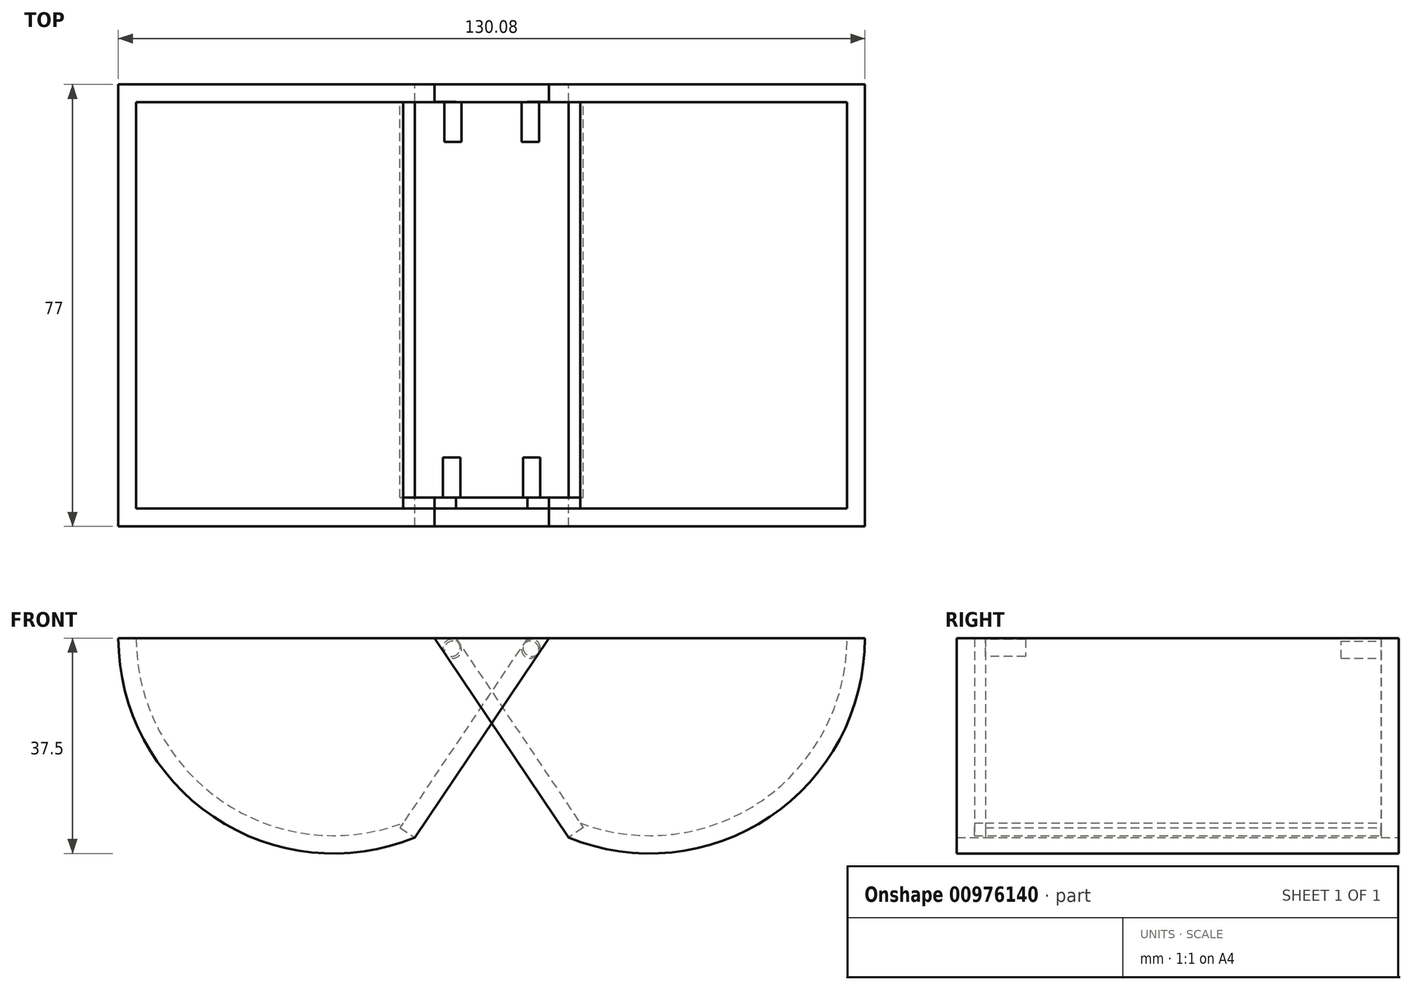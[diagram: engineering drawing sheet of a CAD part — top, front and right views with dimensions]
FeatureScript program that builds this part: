
annotation { "Feature Type Name" : "Feature", "Feature Type Description" : "" }
export const myFeature = defineFeature(function(context is Context, id is Id, definition is map)
    precondition{}
    {
        {
            var Q0;
            Q0=qCreatedBy(makeId("Front.planeOp"),FACE);
            var sketch = newSketch(context, id + "F0", { "sketchPlane" : qUnion([Q0])});
            skArc(sketch, "E0", {"start": v(-65.04, 11.76) * mm, "mid": v(-48.46, -19.36) * mm, "end": v(-13.39, -22.97) * mm});
            skLineSegment(sketch, "E1", {"start": v(-27.54, 11.76) * mm, "end": v(-65.04, 11.76) * mm});
            skLineSegment(sketch, "E2", {"start": v(-65.04, 11.76) * mm, "end": v(9.96, 11.76) * mm});
            skLineSegment(sketch, "E3", {"start": v(9.96, 11.76) * mm, "end": v(-13.39, -22.97) * mm});
            skSolve(sketch);
        }
        {
            var Q0;
            {var subQ0=sQuery(id+"F0.wireOp",EDGE,"E0");Q0=makeQuery(id+"F0.imprint","IMPRINT",FACE,{"disambiguationData":[TD([[makeQuery(id+"F0.imprint","IMPRINT",EDGE,{"derivedFrom":subQ0}),1.0]])]});}
            extrude(context, id + "F1", {"entities" : qUnion([Q0]), "depth" : 77 * mm, "offsetDistance" : 25 * mm});
        }
        {
            var Q0;
            Q0=makeQuery(id+"F1.opExtrude","SWEPT_FACE",FACE,{"disambiguationData":[OSD([sQuery(id+"F0.wireOp",EDGE,"E2")])]});
            shell(context, id + "F2", {"entities" : qUnion([Q0]), "thickness" : 3.1 * mm});
        }
        {
            var Q0;
            Q0=makeQuery(id+"F1.opExtrude","SWEPT_FACE",FACE,{"disambiguationData":[OSD([sQuery(id+"F0.wireOp",EDGE,"E3")])]});
            var sketch = newSketch(context, id + "F3", { "sketchPlane" : qUnion([Q0])});
            skLineSegment(sketch, "E4", {"start": v(-72, 15.31) * mm, "end": v(-72, -26.53) * mm, "construction": true});
            skLineSegment(sketch, "E5", {"start": v(-3, 15.31) * mm, "end": v(-3, -26.53) * mm, "construction": true});
            skLineSegment(sketch, "E6.bottom", {"start": v(-72, 15.31) * mm, "end": v(-3, 15.31) * mm});
            skLineSegment(sketch, "E6.top", {"start": v(-72, -26.53) * mm, "end": v(-3, -26.53) * mm});
            skLineSegment(sketch, "E6.left", {"start": v(-72, 15.31) * mm, "end": v(-72, -26.53) * mm});
            skLineSegment(sketch, "E6.right", {"start": v(-3, 15.31) * mm, "end": v(-3, -26.53) * mm});
            skSolve(sketch);
        }
        {
            var Q0;
            Q0=makeQuery(id+"F3.imprint","IMPRINT",FACE,{"disambiguationData":[TD([[makeQuery(id+"F3.imprint","IMPRINT",EDGE,{"derivedFrom":sQuery(id+"F3.wireOp",EDGE,"E6.bottom")}),-1.0]])]});
            extrude(context, id + "F4", {"entities" : qUnion([Q0]), "operationType" : NewBodyOperationType.REMOVE, "oppositeDirection" : true, "depth" : 3.1 * mm, "offsetDistance" : 25 * mm});
        }
        {
            var Q0;
            Q0=makeQuery(id+"F4.boolean.opBoolean","COPY",FACE,{"derivedFrom":makeQuery(id+"F4.opExtrude","SWEPT_FACE",FACE,{"disambiguationData":[OSD([sQuery(id+"F3.wireOp",EDGE,"E6.left")])]})});
            var sketch = newSketch(context, id + "F5", { "sketchPlane" : qUnion([Q0])});
            skLineSegment(sketch, "E7", {"start": v(-8.84, 10.1) * mm, "end": v(-5.1, 10.1) * mm, "construction": true});
            skLineSegment(sketch, "E8", {"start": v(-8.1, 11.76) * mm, "end": v(-6.98, 10.1) * mm, "construction": true});
            skCircle(sketch, "E9", {"center": v(-6.98, 10.1) * mm, "radius": 1.5 * mm});
            skSolve(sketch);
        }
        {
            var Q0;
            Q0=makeQuery(id+"F4.boolean.opBoolean","COPY",FACE,{"derivedFrom":makeQuery(id+"F4.opExtrude","SWEPT_FACE",FACE,{"disambiguationData":[OSD([sQuery(id+"F3.wireOp",EDGE,"E6.right")])]})});
            var sketch = newSketch(context, id + "F6", { "sketchPlane" : qUnion([Q0])});
            skLineSegment(sketch, "E10", {"start": v(4.88, 9.76) * mm, "end": v(8.61, 9.76) * mm, "construction": true});
            skLineSegment(sketch, "E11", {"start": v(8.1, 11.76) * mm, "end": v(6.75, 9.76) * mm, "construction": true});
            skCircle(sketch, "E12", {"center": v(6.75, 9.76) * mm, "radius": 1.5 * mm});
            skSolve(sketch);
        }
        {
            var Q0;
            Q0=makeQuery(id+"F6.imprint","IMPRINT",FACE,{"disambiguationData":[TD([[makeQuery(id+"F6.imprint","IMPRINT",EDGE,{"derivedFrom":sQuery(id+"F6.wireOp",EDGE,"E12")}),1.0]])]});
            extrude(context, id + "F7", {"entities" : qUnion([Q0]), "operationType" : NewBodyOperationType.ADD, "depth" : 7 * mm, "offsetDistance" : 25 * mm});
        }
        {
            var Q0;
            Q0=makeQuery(id+"F5.imprint","IMPRINT",FACE,{"disambiguationData":[TD([[makeQuery(id+"F5.imprint","IMPRINT",EDGE,{"derivedFrom":sQuery(id+"F5.wireOp",EDGE,"E9")}),1.0]])]});
            extrude(context, id + "F8", {"entities" : qUnion([Q0]), "operationType" : NewBodyOperationType.ADD, "depth" : 7 * mm, "offsetDistance" : 25 * mm});
        }
        {
            var Q0;
            Q0=makeQuery(id+"F1.opExtrude","SWEPT_BODY",BODY,{"disambiguationData":[OSD([sQuery(id+"F0.wireOp",EDGE,"E0"),sQuery(id+"F0.wireOp",EDGE,"E2"),sQuery(id+"F0.wireOp",EDGE,"E3")])]});
            var Q1;
            Q1=qCreatedBy(makeId("Right.planeOp"),FACE);
            mirror(context, id + "F9", {"entities" : qUnion([Q0]), "mirrorPlane" : qUnion([Q1])});
        }
    });
